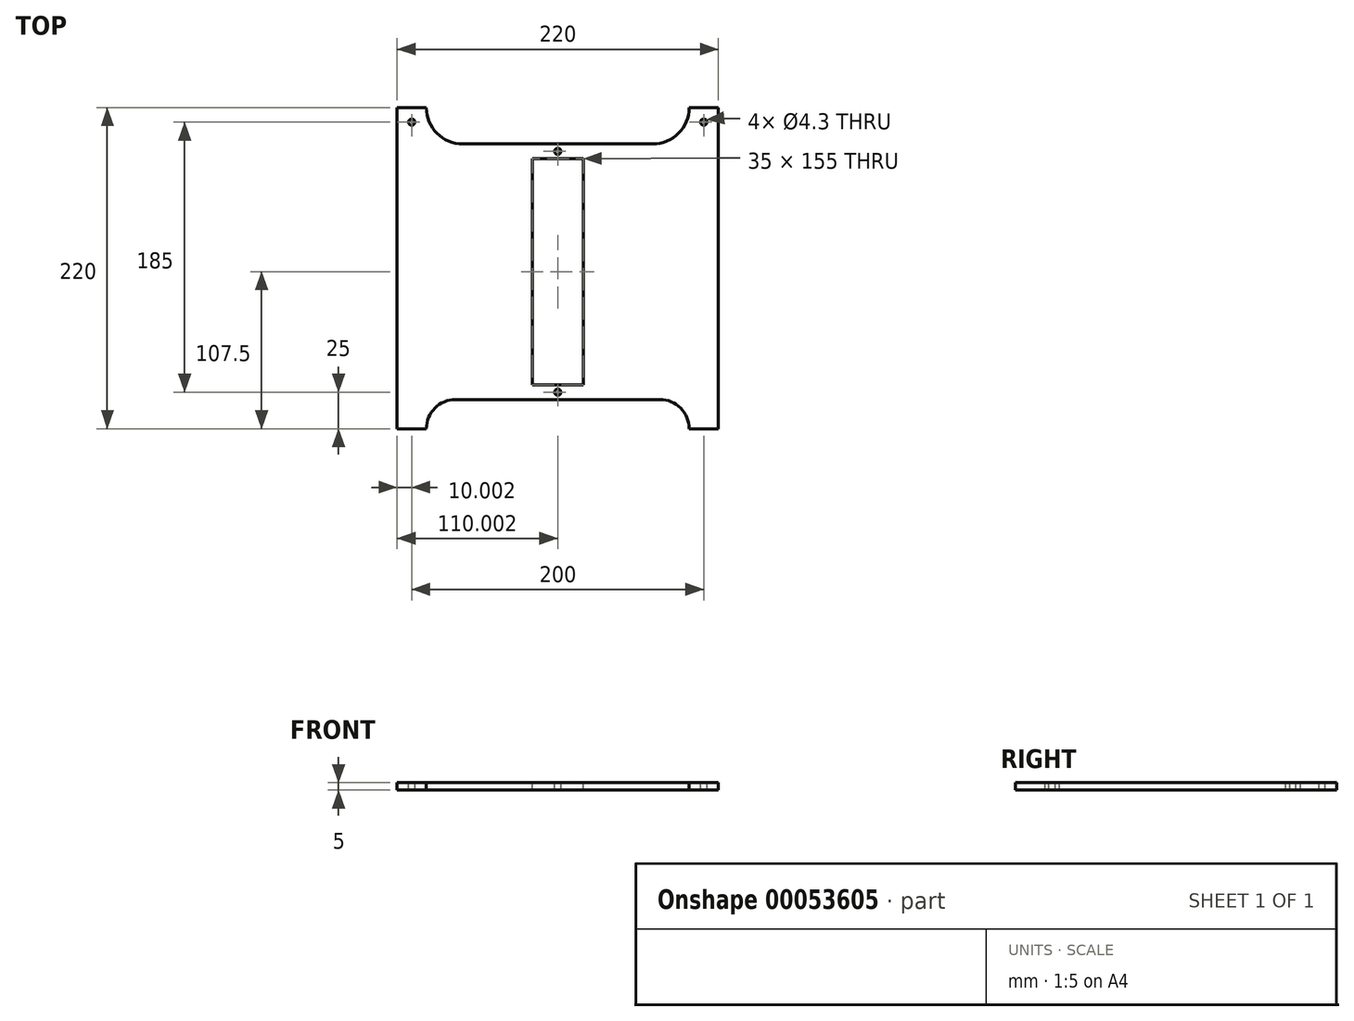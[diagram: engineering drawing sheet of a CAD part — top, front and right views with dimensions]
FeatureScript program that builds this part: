
annotation { "Feature Type Name" : "Feature", "Feature Type Description" : "" }
export const myFeature = defineFeature(function(context is Context, id is Id, definition is map)
    precondition{}
    {
        {
            var Q0;
            Q0=qCreatedBy(makeId("Top.planeOp"),FACE);
            var sketch = newSketch(context, id + "F0", { "sketchPlane" : qUnion([Q0])});
            skLineSegment(sketch, "E0.bottom", {"start": v(-59.59, 113.78) * mm, "end": v(160.41, 113.78) * mm});
            skLineSegment(sketch, "E0.top", {"start": v(-59.59, -106.22) * mm, "end": v(160.41, -106.22) * mm});
            skLineSegment(sketch, "E0.left", {"start": v(-59.59, 113.78) * mm, "end": v(-59.59, -106.22) * mm});
            skLineSegment(sketch, "E0.right", {"start": v(160.41, 113.78) * mm, "end": v(160.41, -106.22) * mm});
            skArc(sketch, "E1", {"start": v(-19.59, -86.22) * mm, "mid": v(-33.73, -92.08) * mm, "end": v(-39.59, -106.22) * mm});
            skArc(sketch, "E2", {"start": v(140.41, -106.22) * mm, "mid": v(134.55, -92.08) * mm, "end": v(120.41, -86.22) * mm});
            skLineSegment(sketch, "E3", {"start": v(-19.59, -86.22) * mm, "end": v(120.41, -86.22) * mm});
            skArc(sketch, "E4", {"start": v(-39.59, 113.78) * mm, "mid": v(-32.27, 96.1) * mm, "end": v(-14.59, 88.78) * mm});
            skArc(sketch, "E5", {"start": v(115.41, 88.78) * mm, "mid": v(133.09, 96.1) * mm, "end": v(140.41, 113.78) * mm});
            skLineSegment(sketch, "E6", {"start": v(-14.59, 88.78) * mm, "end": v(115.41, 88.78) * mm});
            skSolve(sketch);
        }
        {
            var Q0;
            Q0=makeQuery(id+"F0.imprint","IMPRINT",FACE,{"disambiguationData":[TD([[makeQuery(id+"F0.imprint","IMPRINT",EDGE,{"derivedFrom":sQuery(id+"F0.wireOp",EDGE,"E0.bottom")}),-1.0]])]});
            extrude(context, id + "F1", {"entities" : qUnion([Q0]), "depth" : 5 * mm});
        }
        {
            var Q0;
            Q0=makeQuery(id+"F1.opExtrude","CAP_FACE",FACE,{"disambiguationData":[OSD([sQuery(id+"F0.wireOp",EDGE,"E0.bottom"),sQuery(id+"F0.wireOp",EDGE,"E0.top"),sQuery(id+"F0.wireOp",EDGE,"E0.left"),sQuery(id+"F0.wireOp",EDGE,"E0.right"),sQuery(id+"F0.wireOp",EDGE,"E1"),sQuery(id+"F0.wireOp",EDGE,"E2"),sQuery(id+"F0.wireOp",EDGE,"E3")])],"isStart":false});
            var sketch = newSketch(context, id + "F2", { "sketchPlane" : qUnion([Q0])});
            skLineSegment(sketch, "E7.bottom", {"start": v(32.91, -76.22) * mm, "end": v(67.91, -76.22) * mm});
            skLineSegment(sketch, "E7.top", {"start": v(32.91, 78.78) * mm, "end": v(67.91, 78.78) * mm});
            skLineSegment(sketch, "E7.left", {"start": v(32.91, -76.22) * mm, "end": v(32.91, 78.78) * mm});
            skLineSegment(sketch, "E7.right", {"start": v(67.91, -76.22) * mm, "end": v(67.91, 78.78) * mm});
            skPoint(sketch, "E8.centerSnap0", {"position": v(50.41, -86.22) * mm});
            skPoint(sketch, "E9", {"position": v(50.41, 88.78) * mm});
            skSolve(sketch);
        }
        {
            var Q0;
            Q0=makeQuery(id+"F2.imprint","IMPRINT",FACE,{"disambiguationData":[TD([[makeQuery(id+"F2.imprint","IMPRINT",EDGE,{"derivedFrom":sQuery(id+"F2.wireOp",EDGE,"E7.bottom")}),1.0]])]});
            var Q1;
            Q1=makeQuery(id+"F2.imprint","IMPRINT",FACE,{"disambiguationData":[TD([[makeQuery(id+"F2.imprint","IMPRINT",EDGE,{"derivedFrom":sQuery(id+"F2.wireOp",EDGE,"6f018588-a78f-455f-abec-688eab87bc3f")}),1.0]])]});
            var Q2;
            Q2=makeQuery(id+"F2.imprint","IMPRINT",FACE,{"disambiguationData":[TD([[makeQuery(id+"F2.imprint","IMPRINT",EDGE,{"derivedFrom":sQuery(id+"F2.wireOp",EDGE,"E8")}),1.0]])]});
            extrude(context, id + "F3", {"entities" : qUnion([Q0, Q1, Q2]), "operationType" : NewBodyOperationType.REMOVE, "endBound" : BoundingType.THROUGH_ALL, "oppositeDirection" : true, "depth" : 25 * mm});
        }
        {
            var Q0;
            Q0=makeQuery(id+"F1.opExtrude","CAP_FACE",FACE,{"disambiguationData":[OSD([sQuery(id+"F0.wireOp",EDGE,"E0.bottom"),sQuery(id+"F0.wireOp",EDGE,"E0.top"),sQuery(id+"F0.wireOp",EDGE,"E0.left"),sQuery(id+"F0.wireOp",EDGE,"E0.right"),sQuery(id+"F0.wireOp",EDGE,"E1"),sQuery(id+"F0.wireOp",EDGE,"E2"),sQuery(id+"F0.wireOp",EDGE,"E3"),sQuery(id+"F0.wireOp",EDGE,"E4"),sQuery(id+"F0.wireOp",EDGE,"E5"),sQuery(id+"F0.wireOp",EDGE,"E6")])],"isStart":false});
            var sketch = newSketch(context, id + "F4", { "sketchPlane" : qUnion([Q0])});
            skCircle(sketch, "E10", {"center": v(-49.59, 103.78) * mm, "radius": 2.15 * mm});
            skCircle(sketch, "E11", {"center": v(150.41, 103.78) * mm, "radius": 2.15 * mm});
            skCircle(sketch, "E12", {"center": v(50.41, 83.78) * mm, "radius": 2.15 * mm});
            skCircle(sketch, "E13", {"center": v(50.41, -81.22) * mm, "radius": 2.15 * mm});
            skPoint(sketch, "E13.centerSnap0", {"position": v(50.41, -86.22) * mm});
            skPoint(sketch, "E14", {"position": v(50.41, 88.78) * mm});
            skPoint(sketch, "E15", {"position": v(-49.59, 113.78) * mm});
            skPoint(sketch, "E16", {"position": v(150.41, 113.78) * mm});
            skSolve(sketch);
        }
        {
            var Q0;
            Q0 = qSketchRegion(id + "F4", true);
            var Q1;
            Q1 = qSketchRegion(id + "F4", true);
            extrude(context, id + "F5", {"entities" : qUnion([Q0, Q1]), "operationType" : NewBodyOperationType.REMOVE, "endBound" : BoundingType.THROUGH_ALL, "oppositeDirection" : true, "depth" : 25 * mm});
        }
    });
